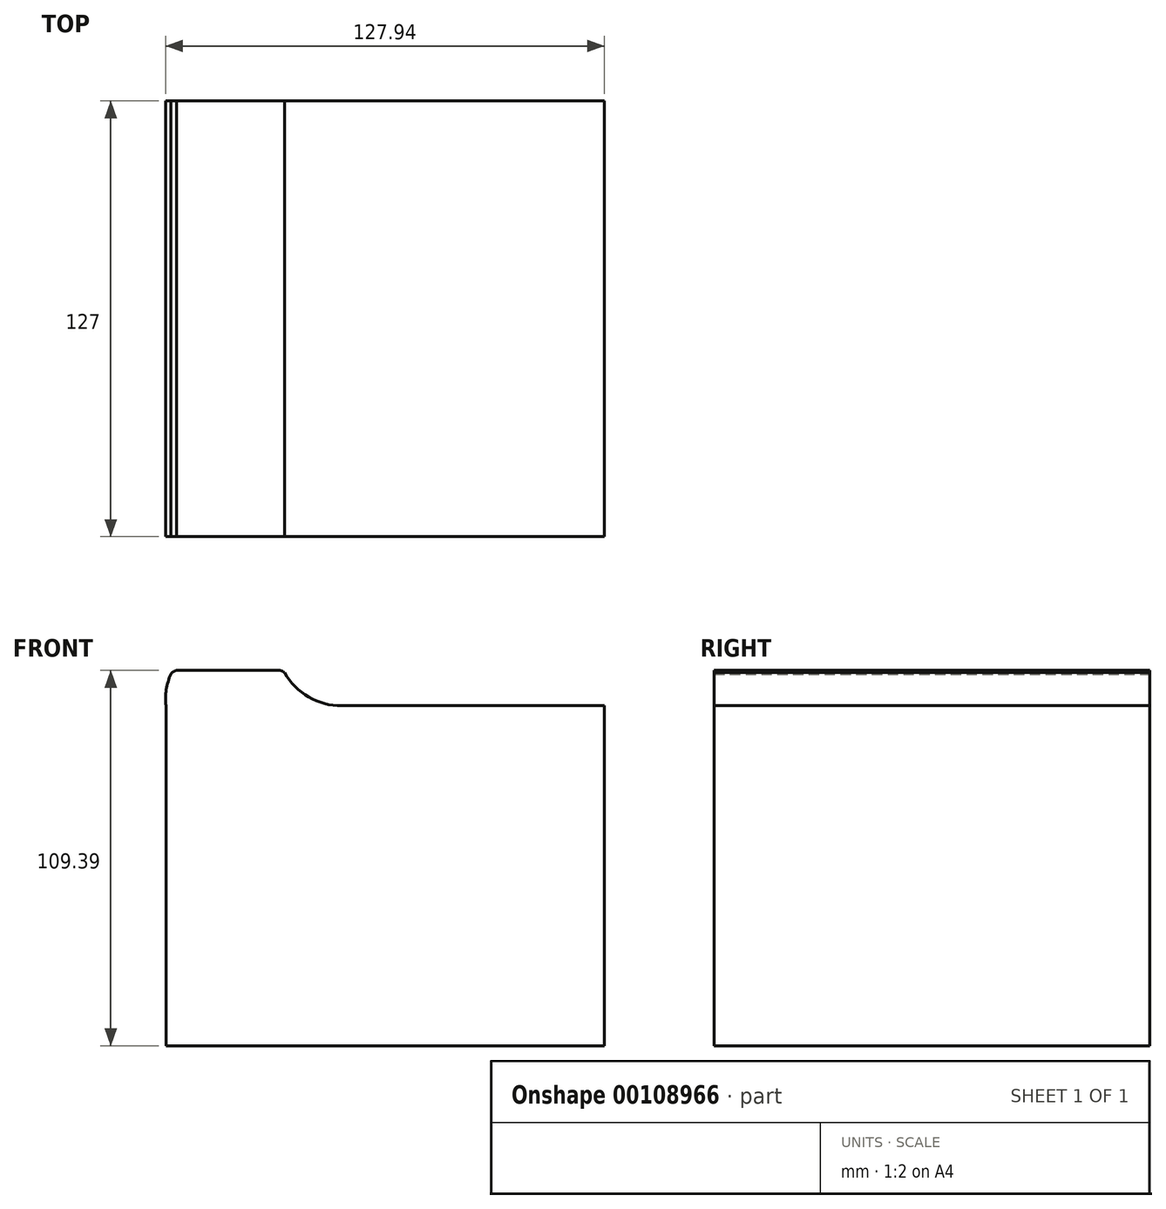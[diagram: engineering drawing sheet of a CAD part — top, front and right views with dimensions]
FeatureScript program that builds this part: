
annotation { "Feature Type Name" : "Feature", "Feature Type Description" : "" }
export const myFeature = defineFeature(function(context is Context, id is Id, definition is map)
    precondition{}
    {
        {
            var Q0;
            Q0=qCreatedBy(makeId("Front.planeOp"),FACE);
            var sketch = newSketch(context, id + "F0", { "sketchPlane" : qUnion([Q0])});
            skLineSegment(sketch, "E0.top", {"start": v(-63.92, -49.54) * mm, "end": v(63.92, -49.54) * mm});
            skLineSegment(sketch, "E0.left", {"start": v(-63.92, 49.54) * mm, "end": v(-63.92, -49.54) * mm});
            skLineSegment(sketch, "E0.right", {"start": v(63.92, 49.54) * mm, "end": v(63.92, -49.54) * mm});
            skPoint(sketch, "E0.middle", {"position": v(0, 0) * mm});
            skLineSegment(sketch, "E1", {"start": v(-29.74, 59.85) * mm, "end": v(-29.74, 59.85) * mm});
            skPoint(sketch, "E2.third.point", {"position": v(-12.84, 49.54) * mm});
            skLineSegment(sketch, "E3.trimOffspring", {"start": v(-12.84, 49.54) * mm, "end": v(63.92, 49.54) * mm});
            skLineSegment(sketch, "E4", {"start": v(-30.9, 59.85) * mm, "end": v(-60.75, 59.85) * mm});
            skArc(sketch, "E5", {"start": v(-62.47, 58.8) * mm, "mid": v(-63.8, 54.27) * mm, "end": v(-63.92, 49.54) * mm});
            skArc(sketch, "E6", {"start": v(-60.75, 59.85) * mm, "mid": v(-61.72, 59.5) * mm, "end": v(-62.47, 58.8) * mm});
            skPoint(sketch, "E6.first.point", {"position": v(-59, 55.3) * mm});
            skPoint(sketch, "E6.second.point", {"position": v(-62.9, 57.76) * mm});
            skPoint(sketch, "E6.third.point", {"position": v(-60.08, 59.85) * mm});
            skArc(sketch, "E7", {"start": v(-29.38, 59.2) * mm, "mid": v(-30.09, 59.68) * mm, "end": v(-30.93, 59.85) * mm});
            skPoint(sketch, "E7.first.point", {"position": v(-32.6, 56.42) * mm});
            skPoint(sketch, "E7.second.point", {"position": v(-29.38, 59.2) * mm});
            skPoint(sketch, "E7.third.point", {"position": v(-30.93, 59.85) * mm});
            skArc(sketch, "E8.trimOffspring", {"start": v(-29.38, 59.2) * mm, "mid": v(-22.33, 52.1) * mm, "end": v(-12.66, 49.54) * mm});
            skSolve(sketch);
        }
        {
            var Q0;
            Q0=makeQuery(id+"F0.imprint","IMPRINT",FACE,{"disambiguationData":[TD([[makeQuery(id+"F0.imprint","IMPRINT",EDGE,{"derivedFrom":sQuery(id+"F0.wireOp",EDGE,"E0.top")}),1.0]])]});
            extrude(context, id + "F1", {"entities" : qUnion([Q0]), "endBound" : BoundingType.SYMMETRIC, "depth" : 127 * mm});
        }
    });
